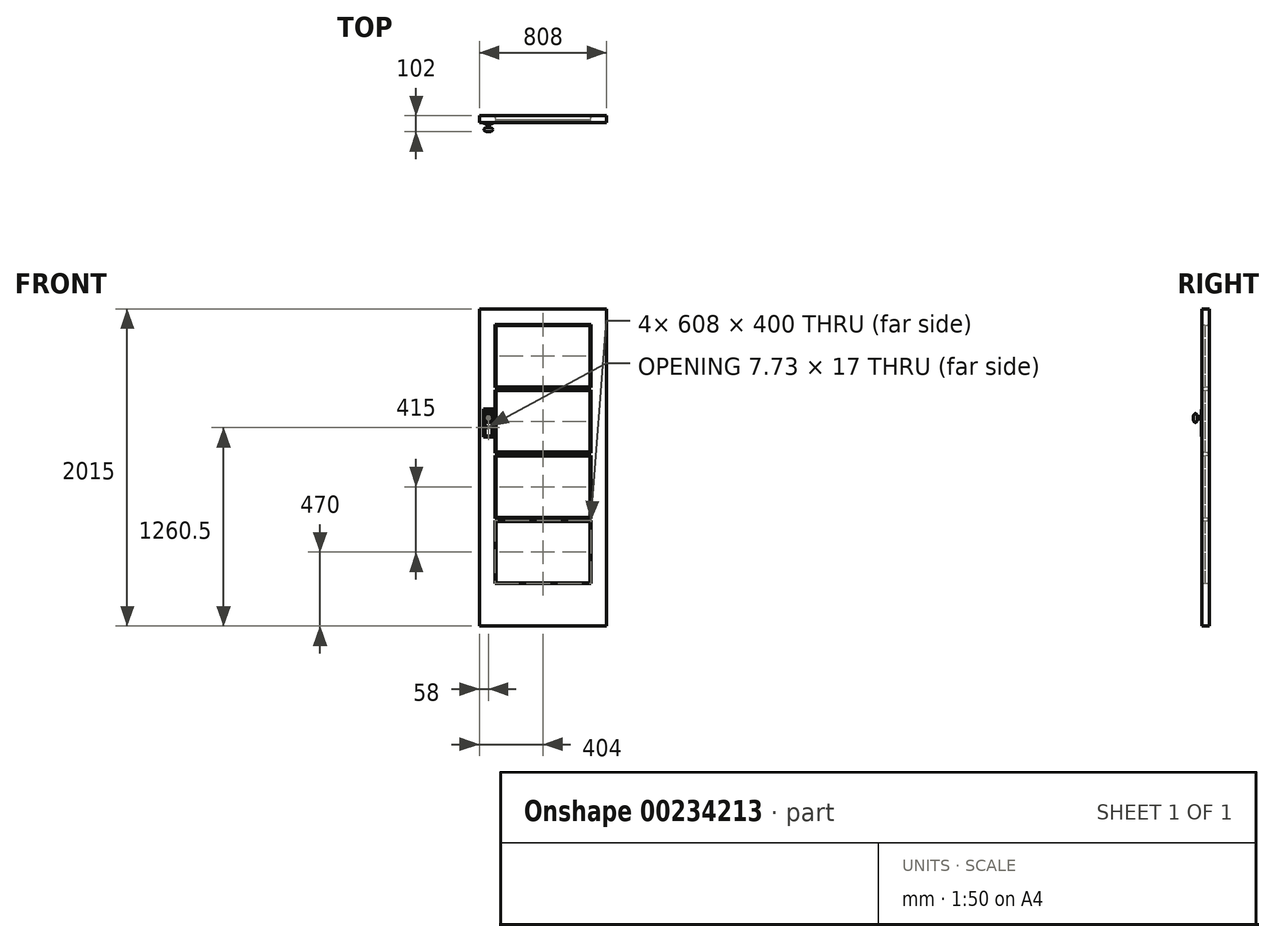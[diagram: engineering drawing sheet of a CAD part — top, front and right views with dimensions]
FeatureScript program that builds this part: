
annotation { "Feature Type Name" : "Feature", "Feature Type Description" : "" }
export const myFeature = defineFeature(function(context is Context, id is Id, definition is map)
    precondition{}
    {
        {
            var Q0;
            Q0=qCreatedBy(makeId("Front.planeOp"),FACE);
            var sketch = newSketch(context, id + "F0", { "sketchPlane" : qUnion([Q0])});
            skLineSegment(sketch, "E0.bottom", {"start": v(0, 0) * mm, "end": v(-808, 0) * mm});
            skLineSegment(sketch, "E0.top", {"start": v(0, 2015) * mm, "end": v(-808, 2015) * mm});
            skLineSegment(sketch, "E0.left", {"start": v(0, 0) * mm, "end": v(0, 2015) * mm});
            skLineSegment(sketch, "E0.right", {"start": v(-808, 0) * mm, "end": v(-808, 2015) * mm});
            skLineSegment(sketch, "E1.bottom", {"start": v(-703, 1910) * mm, "end": v(-105, 1910) * mm});
            skLineSegment(sketch, "E1.top", {"start": v(-703, 1520) * mm, "end": v(-105, 1520) * mm});
            skLineSegment(sketch, "E1.left", {"start": v(-703, 1910) * mm, "end": v(-703, 1520) * mm});
            skLineSegment(sketch, "E1.right", {"start": v(-105, 1910) * mm, "end": v(-105, 1520) * mm});
            skPoint(sketch, "E1.middle", {"position": v(-404, 1715) * mm});
            skLineSegment(sketch, "E2.bottom", {"start": v(-703, 1495) * mm, "end": v(-105, 1495) * mm});
            skLineSegment(sketch, "E2.top", {"start": v(-703, 1105) * mm, "end": v(-105, 1105) * mm});
            skLineSegment(sketch, "E2.left", {"start": v(-703, 1495) * mm, "end": v(-703, 1105) * mm});
            skLineSegment(sketch, "E2.right", {"start": v(-105, 1495) * mm, "end": v(-105, 1105) * mm});
            skPoint(sketch, "E2.middle", {"position": v(-404, 1300) * mm});
            skLineSegment(sketch, "E3.bottom", {"start": v(-703, 1080) * mm, "end": v(-105, 1080) * mm});
            skLineSegment(sketch, "E3.top", {"start": v(-703, 690) * mm, "end": v(-105, 690) * mm});
            skLineSegment(sketch, "E3.left", {"start": v(-703, 1080) * mm, "end": v(-703, 690) * mm});
            skLineSegment(sketch, "E3.right", {"start": v(-105, 1080) * mm, "end": v(-105, 690) * mm});
            skPoint(sketch, "E3.middle", {"position": v(-404, 885) * mm});
            skLineSegment(sketch, "E4.bottom", {"start": v(-703, 275) * mm, "end": v(-105, 275) * mm});
            skLineSegment(sketch, "E4.top", {"start": v(-703, 665) * mm, "end": v(-105, 665) * mm});
            skLineSegment(sketch, "E4.left", {"start": v(-703, 275) * mm, "end": v(-703, 665) * mm});
            skLineSegment(sketch, "E4.right", {"start": v(-105, 275) * mm, "end": v(-105, 665) * mm});
            skPoint(sketch, "E4.middle", {"position": v(-404, 470) * mm});
            skPoint(sketch, "E4.middle.positionSnap0", {"position": v(-404, 690) * mm});
            skPoint(sketch, "E4.centerSnap0", {"position": v(-404, 690) * mm});
            skSolve(sketch);
        }
        {
            var Q0;
            Q0=makeQuery(id+"F0.imprint","IMPRINT",FACE,{"disambiguationData":[TD([[makeQuery(id+"F0.imprint","IMPRINT",EDGE,{"derivedFrom":sQuery(id+"F0.wireOp",EDGE,"E0.bottom")}),-1.0]])]});
            extrude(context, id + "F1", {"entities" : qUnion([Q0]), "depth" : 45 * mm});
        }
        {
            var Q0;
            Q0=makeQuery(id+"F1.opExtrude","CAP_EDGE",EDGE,{"disambiguationData":[OSD([sQuery(id+"F0.wireOp",EDGE,"E4.bottom")])],"isStart":false});
            var Q1;
            Q1=makeQuery(id+"F1.opExtrude","CAP_EDGE",EDGE,{"disambiguationData":[OSD([sQuery(id+"F0.wireOp",EDGE,"E4.right")])],"isStart":false});
            var Q2;
            Q2=makeQuery(id+"F1.opExtrude","CAP_EDGE",EDGE,{"disambiguationData":[OSD([sQuery(id+"F0.wireOp",EDGE,"E4.left")])],"isStart":false});
            var Q3;
            Q3=makeQuery(id+"F1.opExtrude","CAP_EDGE",EDGE,{"disambiguationData":[OSD([sQuery(id+"F0.wireOp",EDGE,"E4.top")])],"isStart":false});
            var Q4;
            Q4=makeQuery(id+"F1.opExtrude","CAP_EDGE",EDGE,{"disambiguationData":[OSD([sQuery(id+"F0.wireOp",EDGE,"E3.left")])],"isStart":false});
            var Q5;
            Q5=makeQuery(id+"F1.opExtrude","CAP_EDGE",EDGE,{"disambiguationData":[OSD([sQuery(id+"F0.wireOp",EDGE,"E3.bottom")])],"isStart":false});
            var Q6;
            Q6=makeQuery(id+"F1.opExtrude","CAP_EDGE",EDGE,{"disambiguationData":[OSD([sQuery(id+"F0.wireOp",EDGE,"E3.top")])],"isStart":false});
            var Q7;
            Q7=makeQuery(id+"F1.opExtrude","CAP_EDGE",EDGE,{"disambiguationData":[OSD([sQuery(id+"F0.wireOp",EDGE,"E3.right")])],"isStart":false});
            var Q8;
            Q8=makeQuery(id+"F1.opExtrude","CAP_EDGE",EDGE,{"disambiguationData":[OSD([sQuery(id+"F0.wireOp",EDGE,"E2.top")])],"isStart":false});
            var Q9;
            Q9=makeQuery(id+"F1.opExtrude","CAP_EDGE",EDGE,{"disambiguationData":[OSD([sQuery(id+"F0.wireOp",EDGE,"E2.right")])],"isStart":false});
            var Q10;
            Q10=makeQuery(id+"F1.opExtrude","CAP_EDGE",EDGE,{"disambiguationData":[OSD([sQuery(id+"F0.wireOp",EDGE,"E2.bottom")])],"isStart":false});
            var Q11;
            Q11=makeQuery(id+"F1.opExtrude","CAP_EDGE",EDGE,{"disambiguationData":[OSD([sQuery(id+"F0.wireOp",EDGE,"E2.left")])],"isStart":false});
            var Q12;
            Q12=makeQuery(id+"F1.opExtrude","CAP_EDGE",EDGE,{"disambiguationData":[OSD([sQuery(id+"F0.wireOp",EDGE,"E1.left")])],"isStart":false});
            var Q13;
            Q13=makeQuery(id+"F1.opExtrude","CAP_EDGE",EDGE,{"disambiguationData":[OSD([sQuery(id+"F0.wireOp",EDGE,"E1.bottom")])],"isStart":false});
            var Q14;
            Q14=makeQuery(id+"F1.opExtrude","CAP_EDGE",EDGE,{"disambiguationData":[OSD([sQuery(id+"F0.wireOp",EDGE,"E1.right")])],"isStart":false});
            var Q15;
            Q15=makeQuery(id+"F1.opExtrude","CAP_EDGE",EDGE,{"disambiguationData":[OSD([sQuery(id+"F0.wireOp",EDGE,"E1.top")])],"isStart":false});
            chamfer(context, id + "F2", {"entities" : qUnion([Q0, Q1, Q2, Q3, Q4, Q5, Q6, Q7, Q8, Q9, Q10, Q11, Q12, Q13, Q14, Q15]), "chamferType" : ChamferType.TWO_OFFSETS, "width1" : 17 * mm, "oppositeDirection" : false, "width2" : 5 * mm, "tangentPropagation" : true});
        }
        {
            var Q0;
            Q0=makeQuery(id+"F1.opExtrude","CAP_EDGE",EDGE,{"disambiguationData":[OSD([sQuery(id+"F0.wireOp",EDGE,"E1.top")])],"isStart":true});
            var Q1;
            Q1=makeQuery(id+"F1.opExtrude","CAP_EDGE",EDGE,{"disambiguationData":[OSD([sQuery(id+"F0.wireOp",EDGE,"E1.right")])],"isStart":true});
            var Q2;
            Q2=makeQuery(id+"F1.opExtrude","CAP_EDGE",EDGE,{"disambiguationData":[OSD([sQuery(id+"F0.wireOp",EDGE,"E1.left")])],"isStart":true});
            var Q3;
            Q3=makeQuery(id+"F1.opExtrude","CAP_EDGE",EDGE,{"disambiguationData":[OSD([sQuery(id+"F0.wireOp",EDGE,"E1.bottom")])],"isStart":true});
            var Q4;
            Q4=makeQuery(id+"F1.opExtrude","CAP_EDGE",EDGE,{"disambiguationData":[OSD([sQuery(id+"F0.wireOp",EDGE,"E2.right")])],"isStart":true});
            var Q5;
            Q5=makeQuery(id+"F1.opExtrude","CAP_EDGE",EDGE,{"disambiguationData":[OSD([sQuery(id+"F0.wireOp",EDGE,"E2.top")])],"isStart":true});
            var Q6;
            Q6=makeQuery(id+"F1.opExtrude","CAP_EDGE",EDGE,{"disambiguationData":[OSD([sQuery(id+"F0.wireOp",EDGE,"E2.bottom")])],"isStart":true});
            var Q7;
            Q7=makeQuery(id+"F1.opExtrude","CAP_EDGE",EDGE,{"disambiguationData":[OSD([sQuery(id+"F0.wireOp",EDGE,"E2.left")])],"isStart":true});
            var Q8;
            Q8=makeQuery(id+"F1.opExtrude","CAP_EDGE",EDGE,{"disambiguationData":[OSD([sQuery(id+"F0.wireOp",EDGE,"E3.bottom")])],"isStart":true});
            var Q9;
            Q9=makeQuery(id+"F1.opExtrude","CAP_EDGE",EDGE,{"disambiguationData":[OSD([sQuery(id+"F0.wireOp",EDGE,"E3.left")])],"isStart":true});
            var Q10;
            Q10=makeQuery(id+"F1.opExtrude","CAP_EDGE",EDGE,{"disambiguationData":[OSD([sQuery(id+"F0.wireOp",EDGE,"E3.right")])],"isStart":true});
            var Q11;
            Q11=makeQuery(id+"F1.opExtrude","CAP_EDGE",EDGE,{"disambiguationData":[OSD([sQuery(id+"F0.wireOp",EDGE,"E3.top")])],"isStart":true});
            var Q12;
            Q12=makeQuery(id+"F1.opExtrude","CAP_EDGE",EDGE,{"disambiguationData":[OSD([sQuery(id+"F0.wireOp",EDGE,"E4.bottom")])],"isStart":true});
            var Q13;
            Q13=makeQuery(id+"F1.opExtrude","CAP_EDGE",EDGE,{"disambiguationData":[OSD([sQuery(id+"F0.wireOp",EDGE,"E4.right")])],"isStart":true});
            var Q14;
            Q14=makeQuery(id+"F1.opExtrude","CAP_EDGE",EDGE,{"disambiguationData":[OSD([sQuery(id+"F0.wireOp",EDGE,"E4.top")])],"isStart":true});
            var Q15;
            Q15=makeQuery(id+"F1.opExtrude","CAP_EDGE",EDGE,{"disambiguationData":[OSD([sQuery(id+"F0.wireOp",EDGE,"E4.left")])],"isStart":true});
            chamfer(context, id + "F3", {"entities" : qUnion([Q0, Q1, Q2, Q3, Q4, Q5, Q6, Q7, Q8, Q9, Q10, Q11, Q12, Q13, Q14, Q15]), "chamferType" : ChamferType.TWO_OFFSETS, "width1" : 25 * mm, "oppositeDirection" : true, "width2" : 5 * mm, "tangentPropagation" : true});
        }
        {
            var Q0;
            Q0=makeQuery(id+"F1.opExtrude","CAP_FACE",FACE,{"disambiguationData":[OSD([sQuery(id+"F0.wireOp",EDGE,"E0.bottom"),sQuery(id+"F0.wireOp",EDGE,"E0.top"),sQuery(id+"F0.wireOp",EDGE,"E0.left"),sQuery(id+"F0.wireOp",EDGE,"E0.right"),sQuery(id+"F0.wireOp",EDGE,"E1.bottom"),sQuery(id+"F0.wireOp",EDGE,"E1.top"),sQuery(id+"F0.wireOp",EDGE,"E1.left"),sQuery(id+"F0.wireOp",EDGE,"E1.right"),sQuery(id+"F0.wireOp",EDGE,"E2.bottom"),sQuery(id+"F0.wireOp",EDGE,"E2.top"),sQuery(id+"F0.wireOp",EDGE,"E2.left"),sQuery(id+"F0.wireOp",EDGE,"E2.right"),sQuery(id+"F0.wireOp",EDGE,"E3.bottom"),sQuery(id+"F0.wireOp",EDGE,"E3.top"),sQuery(id+"F0.wireOp",EDGE,"E3.left"),sQuery(id+"F0.wireOp",EDGE,"E3.right"),sQuery(id+"F0.wireOp",EDGE,"E4.bottom"),sQuery(id+"F0.wireOp",EDGE,"E4.top"),sQuery(id+"F0.wireOp",EDGE,"E4.left"),sQuery(id+"F0.wireOp",EDGE,"E4.right")])],"isStart":false});
            var sketch = newSketch(context, id + "F4", { "sketchPlane" : qUnion([Q0])});
            skLineSegment(sketch, "E5.bottom", {"start": v(-720, 1380) * mm, "end": v(-780, 1380) * mm});
            skLineSegment(sketch, "E5.top", {"start": v(-720, 1200) * mm, "end": v(-780, 1200) * mm});
            skLineSegment(sketch, "E5.left", {"start": v(-720, 1380) * mm, "end": v(-720, 1200) * mm});
            skLineSegment(sketch, "E5.right", {"start": v(-780, 1380) * mm, "end": v(-780, 1200) * mm});
            skArc(sketch, "E6", {"start": v(-748, 1261.54) * mm, "mid": v(-750, 1269) * mm, "end": v(-752, 1261.54) * mm});
            skLineSegment(sketch, "E7", {"start": v(-752, 1261.54) * mm, "end": v(-752.5, 1252) * mm});
            skLineSegment(sketch, "E8", {"start": v(-752.5, 1252) * mm, "end": v(-747.5, 1252) * mm});
            skLineSegment(sketch, "E9", {"start": v(-747.5, 1252) * mm, "end": v(-748, 1261.54) * mm});
            skLineSegment(sketch, "E10", {"start": v(-752, 1261.54) * mm, "end": v(-748, 1261.54) * mm, "construction": true});
            skSolve(sketch);
        }
        {
            var Q0;
            Q0=makeQuery(id+"F4.imprint","IMPRINT",FACE,{"disambiguationData":[TD([[makeQuery(id+"F4.imprint","IMPRINT",EDGE,{"derivedFrom":sQuery(id+"F4.wireOp",EDGE,"E5.bottom")}),1.0]])]});
            extrude(context, id + "F5", {"entities" : qUnion([Q0]), "depth" : 5 * mm});
        }
        {
            var Q0;
            Q0=makeQuery(id+"F5.opExtrude","SWEPT_FACE",FACE,{"disambiguationData":[OSD([sQuery(id+"F4.wireOp",EDGE,"E5.right")])]});
            cPlane(context, id + "F6", {"entities" : qUnion([Q0]), "cplaneType" : CPlaneType.OFFSET, "offset" : 30 * mm, "oppositeDirection" : true, "width" : 150 * mm, "height" : 150 * mm});
        }
        {
            var Q0;
            Q0=qCreatedBy(id+"F6.planeOp",FACE);
            var sketch = newSketch(context, id + "F7", { "sketchPlane" : qUnion([Q0])});
            skEllipticalArc(sketch, "E11", {});
            skLineSegment(sketch, "E12", {"start": v(88, 1322) * mm, "end": v(49.5, 1322) * mm});
            skPoint(sketch, "E12.endSnap0", {"position": v(74, 1322) * mm});
            skLineSegment(sketch, "E13", {"start": v(88, 1322) * mm, "end": v(102, 1322) * mm});
            skLineSegment(sketch, "E14", {"start": v(74.58, 1330) * mm, "end": v(57.5, 1330) * mm});
            skLineSegment(sketch, "E15", {"start": v(49.5, 1330) * mm, "end": v(49.5, 1322) * mm});
            skLineSegment(sketch, "E16", {"start": v(57.5, 1330) * mm, "end": v(49.5, 1334) * mm});
            skLineSegment(sketch, "E17", {"start": v(49.5, 1334) * mm, "end": v(49.5, 1330) * mm});
            const initialGuessF7  = {"E11": [0.088, 1.322, 0, -1, 0.028, 0.014, 1.5707963267948966, 4.422637278948642]};
            skSetInitialGuess(sketch, initialGuessF7);
            skSolve(sketch);
        }
        {
            var Q0;
            Q0=makeQuery(id+"F7.imprint","IMPRINT",FACE,{"disambiguationData":[TD([[makeQuery(id+"F7.imprint","IMPRINT",EDGE,{"derivedFrom":sQuery(id+"F7.wireOp",EDGE,"E11")}),1.0]])]});
            var Q1;
            Q1=sQuery(id+"F7.wireOp",EDGE,"E12");
            revolve(context, id + "F8", {"operationType" : NewBodyOperationType.ADD, "entities" : qUnion([Q0]), "axis" : qUnion([Q1]), "revolveType" : RevolveType.FULL});
        }
        {
            var Q0;
            Q0=makeQuery(id+"F5.opExtrude","CAP_EDGE",EDGE,{"disambiguationData":[OSD([sQuery(id+"F4.wireOp",EDGE,"E5.right")])],"isStart":false});
            var Q1;
            Q1=makeQuery(id+"F5.opExtrude","CAP_EDGE",EDGE,{"disambiguationData":[OSD([sQuery(id+"F4.wireOp",EDGE,"E5.top")])],"isStart":false});
            var Q2;
            Q2=makeQuery(id+"F5.opExtrude","CAP_EDGE",EDGE,{"disambiguationData":[OSD([sQuery(id+"F4.wireOp",EDGE,"E5.left")])],"isStart":false});
            var Q3;
            Q3=makeQuery(id+"F5.opExtrude","CAP_EDGE",EDGE,{"disambiguationData":[OSD([sQuery(id+"F4.wireOp",EDGE,"E5.bottom")])],"isStart":false});
            chamfer(context, id + "F9", {"entities" : qUnion([Q0, Q1, Q2, Q3]), "chamferType" : ChamferType.TWO_OFFSETS, "width1" : 4 * mm, "oppositeDirection" : true, "width2" : 8 * mm, "tangentPropagation" : true});
        }
    });
